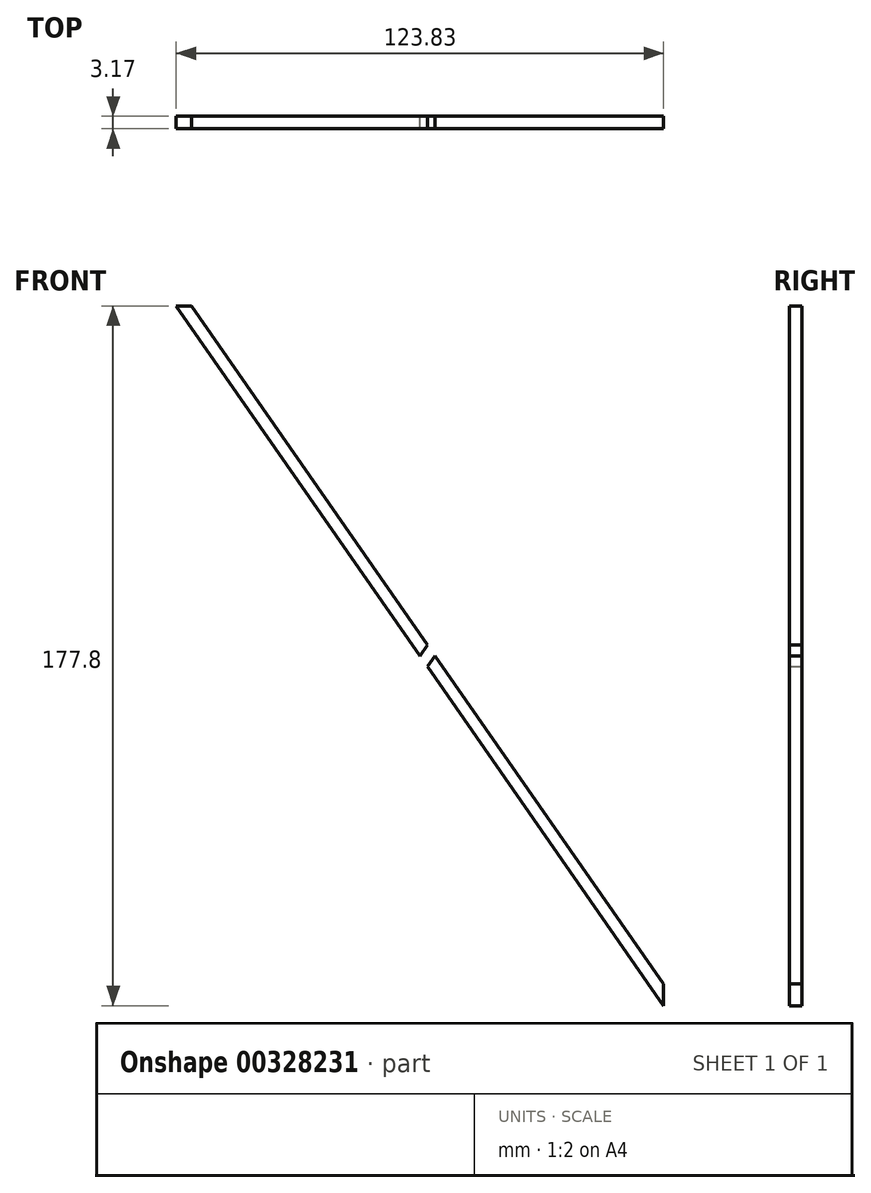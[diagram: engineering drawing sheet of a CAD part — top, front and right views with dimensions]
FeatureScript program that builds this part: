
annotation { "Feature Type Name" : "Feature", "Feature Type Description" : "" }
export const myFeature = defineFeature(function(context is Context, id is Id, definition is map)
    precondition{}
    {
        {
            var Q0;
            Q0=qCreatedBy(makeId("Front.planeOp"),FACE);
            var sketch = newSketch(context, id + "F0", { "sketchPlane" : qUnion([Q0])});
            skLineSegment(sketch, "E0", {"start": v(0, 0) * mm, "end": v(0, 177.8) * mm});
            skLineSegment(sketch, "E1", {"start": v(0, 0) * mm, "end": v(-123.83, 0) * mm});
            skLineSegment(sketch, "E2", {"start": v(-123.83, 0) * mm, "end": v(-123.83, 177.8) * mm});
            skLineSegment(sketch, "E3", {"start": v(-123.83, 177.8) * mm, "end": v(0, 177.8) * mm});
            skLineSegment(sketch, "E4", {"start": v(-123.83, 0) * mm, "end": v(0, 177.8) * mm});
            skLineSegment(sketch, "E5", {"start": v(-119.96, 0) * mm, "end": v(0, 172.24) * mm});
            skLineSegment(sketch, "E6", {"start": v(0, 172.24) * mm, "end": v(0, 177.8) * mm});
            skLineSegment(sketch, "E7", {"start": v(-119.96, 0) * mm, "end": v(-123.83, 0) * mm});
            skLineSegment(sketch, "E8", {"start": v(-123.83, 177.8) * mm, "end": v(-61.91, 88.9) * mm});
            skLineSegment(sketch, "E9", {"start": v(-59.98, 86.12) * mm, "end": v(0, 0) * mm});
            skLineSegment(sketch, "E10", {"start": v(-119.96, 177.8) * mm, "end": v(-59.98, 91.68) * mm});
            skLineSegment(sketch, "E11", {"start": v(0, 5.56) * mm, "end": v(-58.04, 88.9) * mm});
            skLineSegment(sketch, "E12", {"start": v(-58.04, 88.9) * mm, "end": v(-59.98, 86.12) * mm});
            skLineSegment(sketch, "E13", {"start": v(0, 0) * mm, "end": v(0, 5.56) * mm});
            skLineSegment(sketch, "E14", {"start": v(-123.83, 177.8) * mm, "end": v(-119.96, 177.8) * mm});
            skLineSegment(sketch, "E15", {"start": v(-61.91, 88.9) * mm, "end": v(-59.98, 91.68) * mm});
            skSolve(sketch);
        }
        {
            var Q0;
            Q0=makeQuery(id+"F0.imprint","IMPRINT",FACE,{"disambiguationData":[TD([[makeQuery(id+"F0.imprint","IMPRINT",EDGE,{"derivedFrom":sQuery(id+"F0.wireOp",EDGE,"E8")}),1.0]])]});
            var Q1;
            Q1=makeQuery(id+"F0.imprint","IMPRINT",FACE,{"disambiguationData":[TD([[makeQuery(id+"F0.imprint","IMPRINT",EDGE,{"derivedFrom":sQuery(id+"F0.wireOp",EDGE,"E9")}),1.0]])]});
            var Q2;
            {var subQ0=sQuery(id+"F0.wireOp",EDGE,"E6");Q2=makeQuery(id+"F0.imprint","IMPRINT",FACE,{"disambiguationData":[TD([[makeQuery(id+"F0.imprint","IMPRINT",EDGE,{"derivedFrom":subQ0}),1.0]])]});}
            extrude(context, id + "F1", {"entities" : qUnion([Q0, Q1, Q2]), "depth" : 3.17 * mm});
        }
    });
